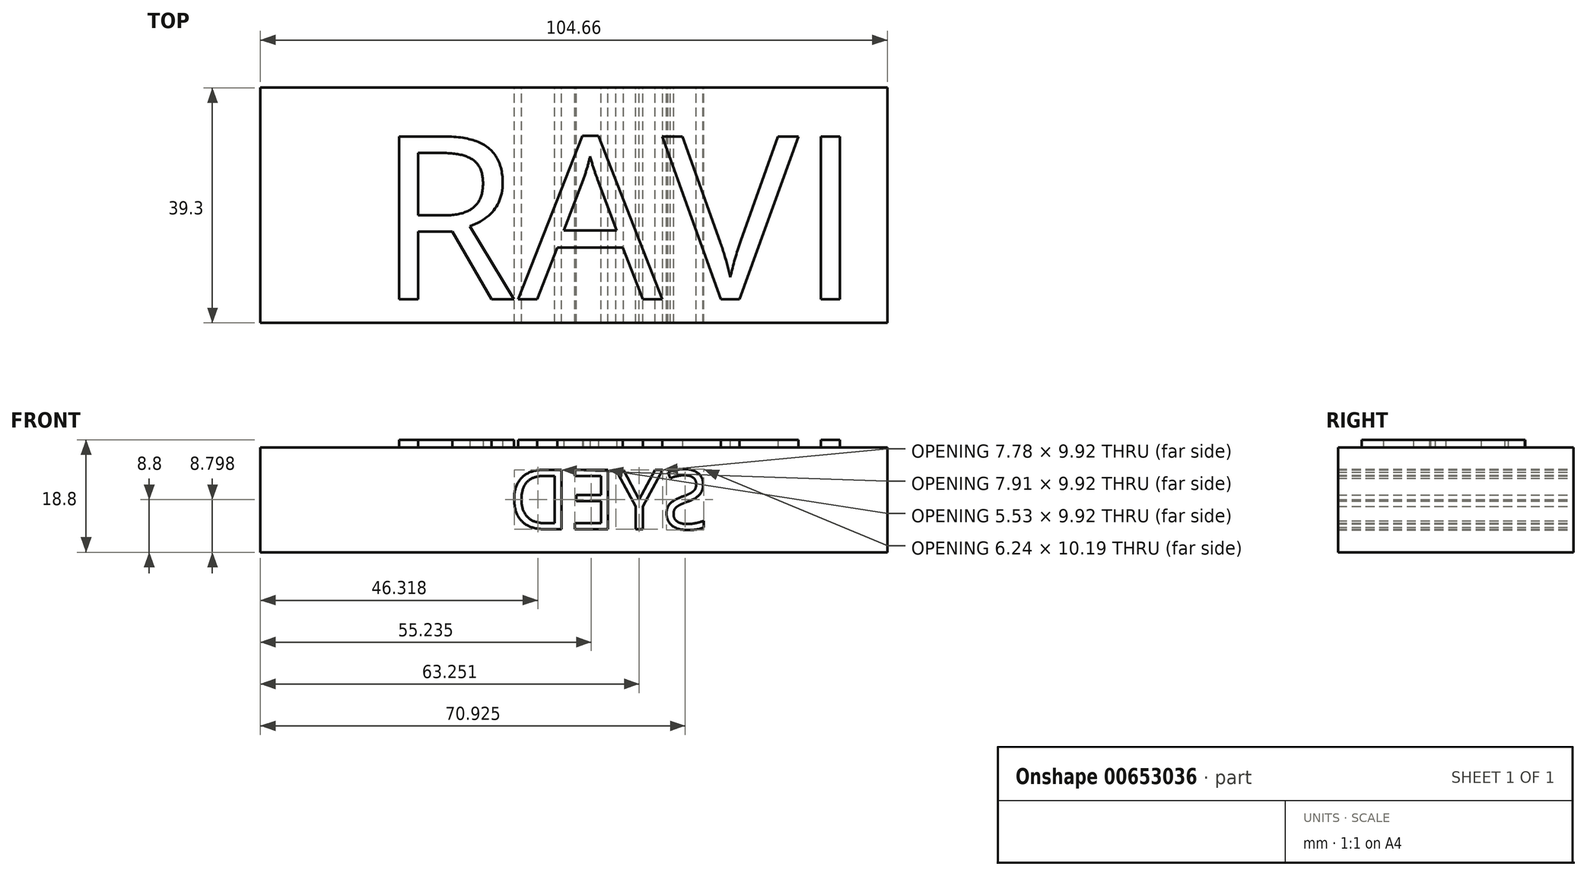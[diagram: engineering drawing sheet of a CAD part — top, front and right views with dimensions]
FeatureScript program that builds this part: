
annotation { "Feature Type Name" : "Feature", "Feature Type Description" : "" }
export const myFeature = defineFeature(function(context is Context, id is Id, definition is map)
    precondition{}
    {
        {
            var Q0;
            Q0=qCreatedBy(makeId("Top.planeOp"),FACE);
            var sketch = newSketch(context, id + "F0", { "sketchPlane" : qUnion([Q0])});
            skLineSegment(sketch, "E0.bottom", {"start": v(-34.07, -11.51) * mm, "end": v(70.6, -11.51) * mm});
            skLineSegment(sketch, "E0.top", {"start": v(-34.07, 27.8) * mm, "end": v(70.6, 27.8) * mm});
            skLineSegment(sketch, "E0.left", {"start": v(-34.07, -11.51) * mm, "end": v(-34.07, 27.8) * mm});
            skLineSegment(sketch, "E0.right", {"start": v(70.6, -11.51) * mm, "end": v(70.6, 27.8) * mm});
            skSolve(sketch);
        }
        {
            var Q0;
            Q0=makeQuery(id+"F0.imprint","IMPRINT",FACE,{"disambiguationData":[TD([[makeQuery(id+"F0.imprint","IMPRINT",EDGE,{"derivedFrom":sQuery(id+"F0.wireOp",EDGE,"E0.bottom")}),1.0]])]});
            extrude(context, id + "F1", {"entities" : qUnion([Q0]), "depth" : 17.53 * mm, "offsetDistance" : 25.4 * mm});
        }
        {
            var Q0;
            Q0=makeQuery(id+"F1.opExtrude","CAP_FACE",FACE,{"disambiguationData":[OSD([sQuery(id+"F0.wireOp",EDGE,"E0.bottom"),sQuery(id+"F0.wireOp",EDGE,"E0.top"),sQuery(id+"F0.wireOp",EDGE,"E0.left"),sQuery(id+"F0.wireOp",EDGE,"E0.right")])],"isStart":false});
            var sketch = newSketch(context, id + "F2", { "sketchPlane" : qUnion([Q0])});
            skText(sketch, "E1", { "text": " RAVI\n", "fontName": "OpenSans-Regular.ttf"});
            const initialGuessF2  = {"E1": [-0.02454, -0.00756, 1, 0, 0.02745]};
            skSetInitialGuess(sketch, initialGuessF2);
            skSolve(sketch);
        }
        {
            var Q0;
            Q0 = qSketchRegion(id + "F2", true);
            extrude(context, id + "F3", {"entities" : qUnion([Q0]), "operationType" : NewBodyOperationType.ADD, "depth" : 1.27 * mm, "offsetDistance" : 25.4 * mm});
        }
        {
            var Q0;
            Q0=makeQuery(id+"F1.opExtrude","SWEPT_FACE",FACE,{"disambiguationData":[OSD([sQuery(id+"F0.wireOp",EDGE,"E0.top")])]});
            var sketch = newSketch(context, id + "F4", { "sketchPlane" : qUnion([Q0])});
            skText(sketch, "E2", { "text": "   SYED", "fontName": "OpenSans-Regular.ttf"});
            const initialGuessF4  = {"E2": [-0.05152, 0.00384, 1, 0, 0.01]};
            skSetInitialGuess(sketch, initialGuessF4);
            skSolve(sketch);
        }
        {
            var Q0;
            Q0 = qSketchRegion(id + "F4", true);
            extrude(context, id + "F5", {"entities" : qUnion([Q0]), "operationType" : NewBodyOperationType.REMOVE, "endBound" : BoundingType.THROUGH_ALL, "oppositeDirection" : true, "depth" : 25.4 * mm, "offsetDistance" : 25.4 * mm});
        }
    });
